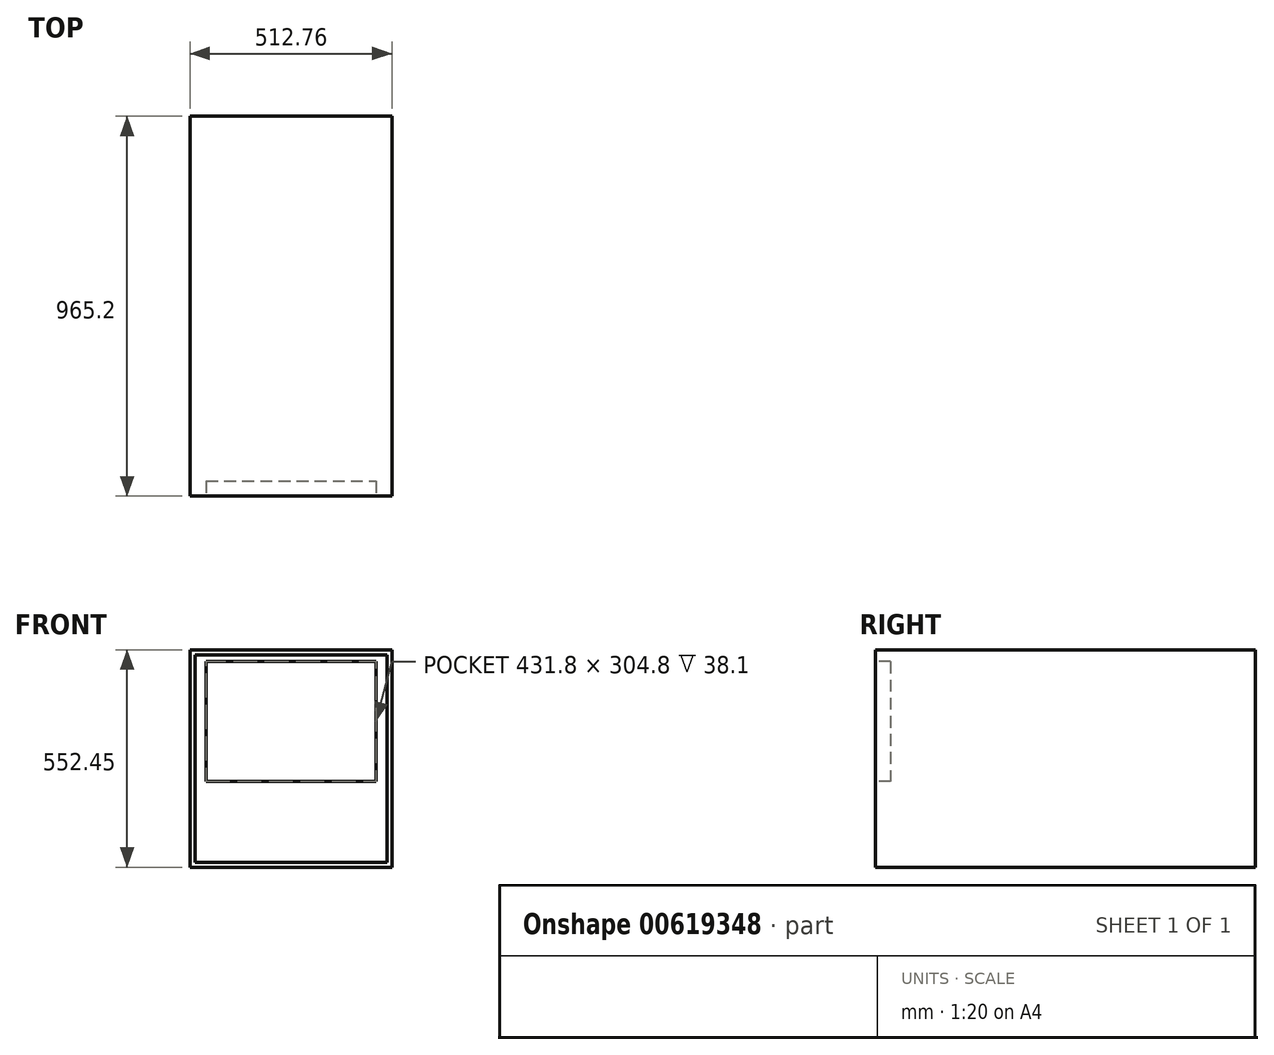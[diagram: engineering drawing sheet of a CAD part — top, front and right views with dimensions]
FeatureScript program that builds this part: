
annotation { "Feature Type Name" : "Feature", "Feature Type Description" : "" }
export const myFeature = defineFeature(function(context is Context, id is Id, definition is map)
    precondition{}
    {
        {
            var Q0;
            Q0=qCreatedBy(makeId("Front.planeOp"),FACE);
            var sketch = newSketch(context, id + "F0", { "sketchPlane" : qUnion([Q0])});
            skLineSegment(sketch, "E0.bottom", {"start": v(-256.38, 173.04) * mm, "end": v(256.38, 173.04) * mm});
            skLineSegment(sketch, "E0.top", {"start": v(-256.38, -379.41) * mm, "end": v(256.38, -379.41) * mm});
            skLineSegment(sketch, "E0.left", {"start": v(-256.38, 173.04) * mm, "end": v(-256.38, -379.41) * mm});
            skLineSegment(sketch, "E0.right", {"start": v(256.38, 173.04) * mm, "end": v(256.38, -379.41) * mm});
            skSolve(sketch);
        }
        {
            var Q0;
            Q0=makeQuery(id+"F0.imprint","IMPRINT",FACE,{"disambiguationData":[TD([[makeQuery(id+"F0.imprint","IMPRINT",EDGE,{"derivedFrom":sQuery(id+"F0.wireOp",EDGE,"E0.bottom")}),-1.0]])]});
            extrude(context, id + "F1", {"entities" : qUnion([Q0]), "oppositeDirection" : true, "depth" : 965.2 * mm, "offsetDistance" : 25.4 * mm});
        }
        {
            var Q0;
            Q0=makeQuery(id+"F1.opExtrude","CAP_FACE",FACE,{"disambiguationData":[OSD([sQuery(id+"F0.wireOp",EDGE,"E0.bottom"),sQuery(id+"F0.wireOp",EDGE,"E0.top"),sQuery(id+"F0.wireOp",EDGE,"E0.left"),sQuery(id+"F0.wireOp",EDGE,"E0.right")])],"isStart":true});
            var sketch = newSketch(context, id + "F2", { "sketchPlane" : qUnion([Q0])});
            skLineSegment(sketch, "E1.bottom", {"start": v(-243.68, 160.34) * mm, "end": v(243.68, 160.34) * mm});
            skLineSegment(sketch, "E1.top", {"start": v(-243.68, -366.71) * mm, "end": v(243.68, -366.71) * mm});
            skLineSegment(sketch, "E1.left", {"start": v(-243.68, 160.34) * mm, "end": v(-243.68, -366.71) * mm});
            skLineSegment(sketch, "E1.right", {"start": v(243.68, 160.34) * mm, "end": v(243.68, -366.71) * mm});
            skSolve(sketch);
        }
        {
            var Q0;
            Q0 = qSketchRegion(id + "F2", true);
            extrude(context, id + "F3", {"entities" : qUnion([Q0]), "operationType" : NewBodyOperationType.REMOVE, "oppositeDirection" : true, "depth" : 0.5 * mm, "offsetDistance" : 25.4 * mm});
        }
        {
            var Q0;
            Q0=makeQuery(id+"F3.boolean.opBoolean","COPY",FACE,{"derivedFrom":makeQuery(id+"F3.opExtrude","CAP_FACE",FACE,{"disambiguationData":[OSD([sQuery(id+"F2.wireOp",EDGE,"E1.bottom"),sQuery(id+"F2.wireOp",EDGE,"E1.top"),sQuery(id+"F2.wireOp",EDGE,"E1.left"),sQuery(id+"F2.wireOp",EDGE,"E1.right")])],"isStart":false})});
            var sketch = newSketch(context, id + "F4", { "sketchPlane" : qUnion([Q0])});
            skLineSegment(sketch, "E2.bottom", {"start": v(-215.9, 142.87) * mm, "end": v(215.9, 142.88) * mm});
            skLineSegment(sketch, "E2.top", {"start": v(-215.9, -161.93) * mm, "end": v(215.9, -161.93) * mm});
            skLineSegment(sketch, "E2.left", {"start": v(-215.9, 142.88) * mm, "end": v(-215.9, -161.92) * mm});
            skLineSegment(sketch, "E2.right", {"start": v(215.9, 142.88) * mm, "end": v(215.9, -161.93) * mm});
            skSolve(sketch);
        }
        {
            var Q0;
            Q0=makeQuery(id+"F4.imprint","IMPRINT",FACE,{"disambiguationData":[TD([[makeQuery(id+"F4.imprint","IMPRINT",EDGE,{"derivedFrom":sQuery(id+"F4.wireOp",EDGE,"E2.bottom")}),-1.0]])]});
            extrude(context, id + "F5", {"entities" : qUnion([Q0]), "operationType" : NewBodyOperationType.REMOVE, "oppositeDirection" : true, "depth" : 38.1 * mm, "offsetDistance" : 25.4 * mm});
        }
        {
            var Q0;
            Q0=makeQuery(id+"F5.boolean.opBoolean","COPY",FACE,{"derivedFrom":makeQuery(id+"F5.opExtrude","CAP_FACE",FACE,{"disambiguationData":[OSD([sQuery(id+"F4.wireOp",EDGE,"E2.bottom"),sQuery(id+"F4.wireOp",EDGE,"E2.top"),sQuery(id+"F4.wireOp",EDGE,"E2.left"),sQuery(id+"F4.wireOp",EDGE,"E2.right")])],"isStart":false})});
            extrude(context, id + "F6", {"entities" : qUnion([Q0]), "depth" : 0.25 * mm, "offsetDistance" : 25.4 * mm});
        }
    });
